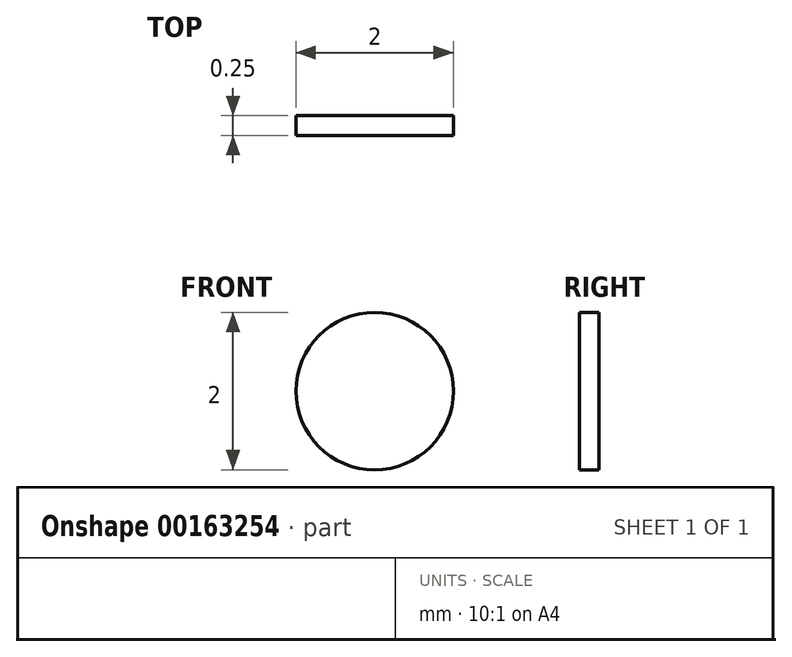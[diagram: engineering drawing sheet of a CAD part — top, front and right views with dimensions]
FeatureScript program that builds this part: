
annotation { "Feature Type Name" : "Feature", "Feature Type Description" : "" }
export const myFeature = defineFeature(function(context is Context, id is Id, definition is map)
    precondition{}
    {
        {
            var Q0;
            Q0=qCreatedBy(makeId("Front.planeOp"),FACE);
            var sketch = newSketch(context, id + "F0", { "sketchPlane" : qUnion([Q0])});
            skCircle(sketch, "E0", {"center": v(0, 0) * mm, "radius": 1 * mm});
            skSolve(sketch);
        }
        {
            var Q0;
            Q0 = qSketchRegion(id + "F0", true);
            extrude(context, id + "F1", {"entities" : qUnion([Q0]), "depth" : .25 * mm});
        }
    });
